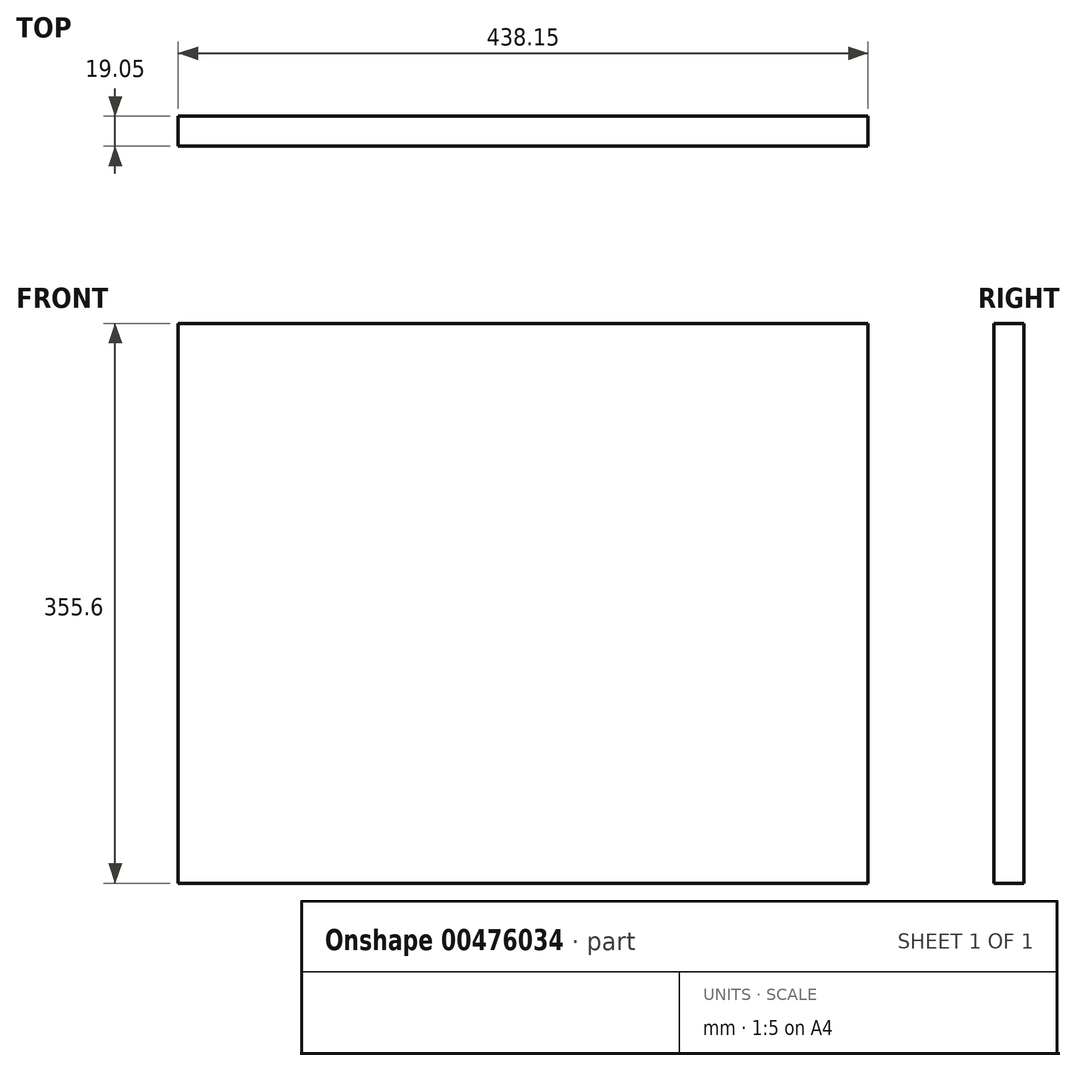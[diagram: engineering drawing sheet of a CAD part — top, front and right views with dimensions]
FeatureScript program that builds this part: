
annotation { "Feature Type Name" : "Feature", "Feature Type Description" : "" }
export const myFeature = defineFeature(function(context is Context, id is Id, definition is map)
    precondition{}
    {
        {
            var Q0;
            Q0=qCreatedBy(makeId("Front.planeOp"),FACE);
            var sketch = newSketch(context, id + "F0", { "sketchPlane" : qUnion([Q0])});
            skLineSegment(sketch, "E0.bottom", {"start": v(0, 0) * mm, "end": v(438.15, 0) * mm});
            skLineSegment(sketch, "E0.top", {"start": v(0, 355.6) * mm, "end": v(438.15, 355.6) * mm});
            skLineSegment(sketch, "E0.left", {"start": v(0, 0) * mm, "end": v(0, 355.6) * mm});
            skLineSegment(sketch, "E0.right", {"start": v(438.15, 0) * mm, "end": v(438.15, 355.6) * mm});
            skLineSegment(sketch, "E1.bottom", {"start": v(211.61, -37.98) * mm, "end": v(219.75, -37.98) * mm});
            skLineSegment(sketch, "E1.top", {"start": v(211.61, -115.3) * mm, "end": v(219.75, -115.3) * mm});
            skLineSegment(sketch, "E1.left", {"start": v(211.61, -37.98) * mm, "end": v(211.61, -115.3) * mm});
            skLineSegment(sketch, "E1.right", {"start": v(219.75, -37.98) * mm, "end": v(219.75, -115.3) * mm});
            skSolve(sketch);
        }
        {
            var Q0;
            Q0 = qSketchRegion(id + "F0", true);
            extrude(context, id + "F1", {"entities" : qUnion([Q0]), "depth" : 19.05 * mm});
        }
        {
            var Q0;
            Q0=makeQuery(id+"F1.opExtrude","SWEPT_BODY",BODY,{"disambiguationData":[OSD([sQuery(id+"F0.wireOp",EDGE,"E1.bottom"),sQuery(id+"F0.wireOp",EDGE,"E1.top"),sQuery(id+"F0.wireOp",EDGE,"E1.left"),sQuery(id+"F0.wireOp",EDGE,"E1.right")])]});
            deleteBodies(context, id + "F2", {"entities" : qUnion([Q0])});
        }
    });
